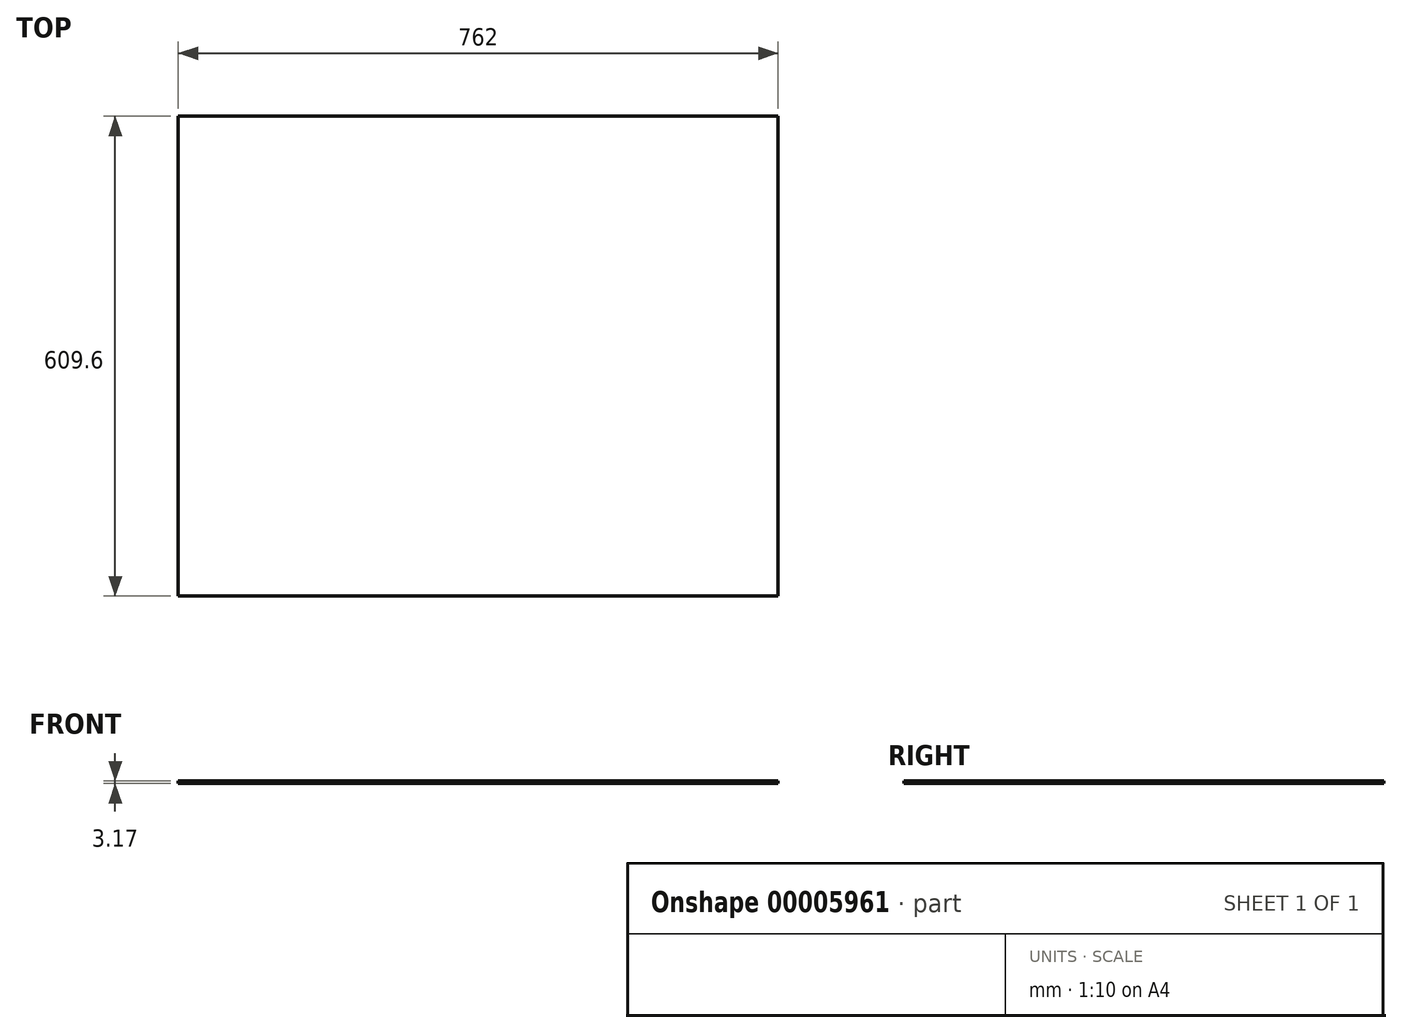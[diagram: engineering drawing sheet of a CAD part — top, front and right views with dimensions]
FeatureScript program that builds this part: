
annotation { "Feature Type Name" : "Feature", "Feature Type Description" : "" }
export const myFeature = defineFeature(function(context is Context, id is Id, definition is map)
    precondition{}
    {
        {
            var Q0;
            Q0=qCreatedBy(makeId("Top.planeOp"),FACE);
            var sketch = newSketch(context, id + "F0", { "sketchPlane" : qUnion([Q0])});
            skLineSegment(sketch, "E0.bottom", {"start": v(-399.76, 486.73) * mm, "end": v(362.24, 486.73) * mm});
            skLineSegment(sketch, "E0.top", {"start": v(-399.76, -122.87) * mm, "end": v(362.24, -122.87) * mm});
            skLineSegment(sketch, "E0.left", {"start": v(-399.76, 486.73) * mm, "end": v(-399.76, -122.87) * mm});
            skLineSegment(sketch, "E0.right", {"start": v(362.24, 486.73) * mm, "end": v(362.24, -122.87) * mm});
            skSolve(sketch);
        }
        {
            var Q0;
            Q0=qSketchRegion(id+"F0",true);
            extrude(context, id + "F1", {"entities" : qUnion([Q0]), "depth" : 3.17 * mm});
        }
    });
